# Revit family: 201_OKA-P-_
name_source: partatom
category: Air Terminals
units: mm (PartAtom-declared; Revit-internal decimal feet)

## family parameters
Always vertical = Yes
Cut with Voids When Loaded = No
Part Type = Normal
Room Calculation Point = Yes
Round Connector Dimension = Use Diameter
Shared = No
Work Plane-Based = No

## types (2) — shared parameters
A = 205 mm  [stored 0.672572 ft]
CAT0 = Yes
CL_Location_5000 = 5000 mm  [stored 16.4042 ft]
CON1 = Yes
CON2 = No
CON3 = No
CON4 = No
Description = Air terminal device for smoke control
L1 = 45 mm  [stored 0.147638 ft]
L_ARR = 400 mm  [stored 1.31234 ft]
Manufacturer = Climecon
QmdConnectorList = 201;D
R = 5 mm  [stored 0.0164042 ft]
URL = www.climecon.fi
W_ARR = 400 mm  [stored 1.31234 ft]
magiPartTypeId = 201
magiProductFamilyId = OKA-P-*
zero-valued in all types: CLBTZ, H_ARR

## per-type parameters (varying)
| type | D | EX | EX__ve |
| OKA-P-100 | 100 mm | 35 mm | -35 mm |
| OKA-P-125 | 125 mm | 44 mm  [stored 0.144357 ft] | -44 mm  [stored -0.144357 ft] |

note: column(s) folded — value = type name in every type: MC Product Code, magiProductId

note: [stored X ft] marks values corroborated as IEEE doubles in the binary element streams (Revit-internal decimal feet)

## geometry (parser evidence)
native form markers: Sweep x1
no freeform markers — native parametric forms only
